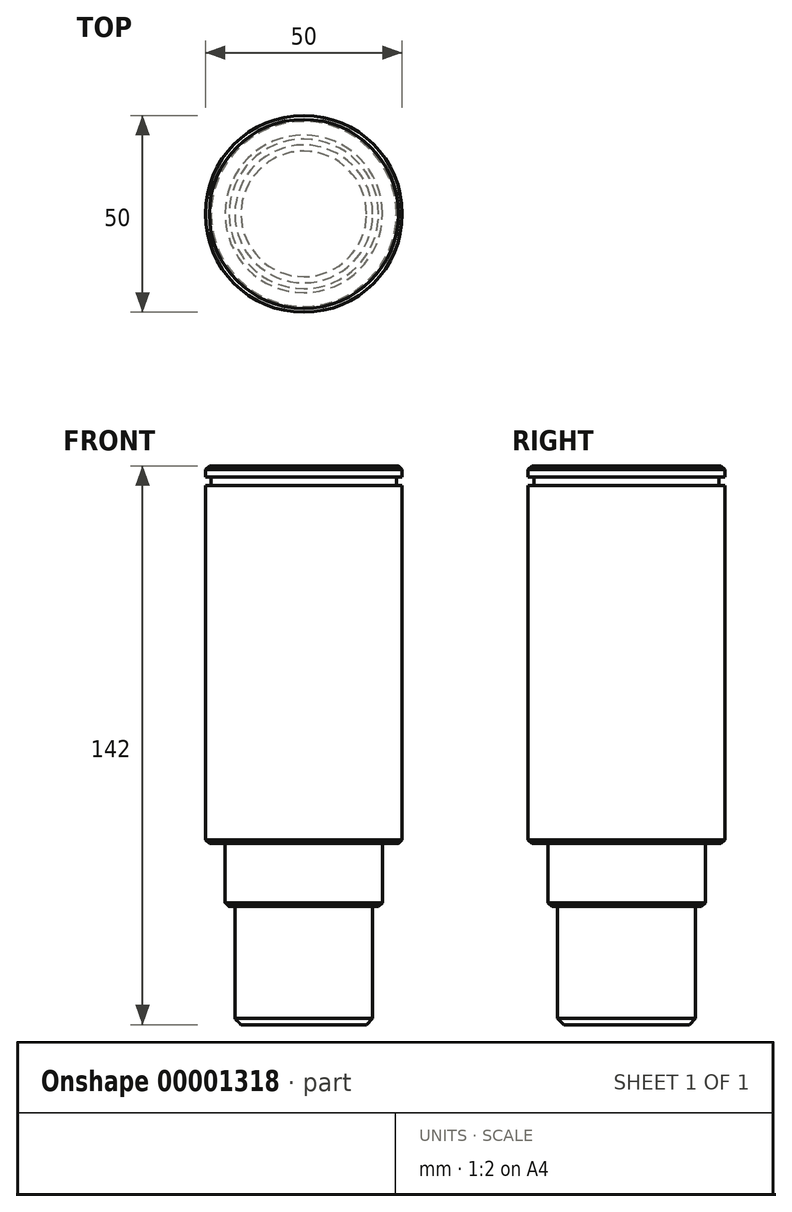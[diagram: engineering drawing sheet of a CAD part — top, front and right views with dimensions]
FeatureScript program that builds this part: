
annotation { "Feature Type Name" : "Feature", "Feature Type Description" : "" }
export const myFeature = defineFeature(function(context is Context, id is Id, definition is map)
    precondition{}
    {
        {
            var Q0;
            Q0=qCreatedBy(makeId("Top.planeOp"),FACE);
            var sketch = newSketch(context, id + "F0", { "sketchPlane" : qUnion([Q0])});
            skCircle(sketch, "E0", {"center": v(0, 0) * mm, "radius": 25 * mm});
            skSolve(sketch);
        }
        {
            var Q0;
            Q0=makeQuery(id+"F0.imprint","IMPRINT",FACE,{"disambiguationData":[TD([[makeQuery(id+"F0.imprint","IMPRINT",EDGE,{"derivedFrom":sQuery(id+"F0.wireOp",EDGE,"E0")}),1.0]])]});
            extrude(context, id + "F1", {"entities" : qUnion([Q0]), "depth" : 91 * mm});
        }
        {
            var Q0;
            Q0=makeQuery(id+"F1.opExtrude","CAP_FACE",FACE,{"disambiguationData":[OSD([sQuery(id+"F0.wireOp",EDGE,"E0")])],"isStart":false});
            var sketch = newSketch(context, id + "F2", { "sketchPlane" : qUnion([Q0])});
            skCircle(sketch, "E1", {"center": v(0, 0) * mm, "radius": 23.5 * mm});
            skSolve(sketch);
        }
        {
            var Q0;
            Q0=makeQuery(id+"F2.imprint","IMPRINT",FACE,{"disambiguationData":[TD([[makeQuery(id+"F2.imprint","IMPRINT",EDGE,{"derivedFrom":sQuery(id+"F2.wireOp",EDGE,"E1")}),1.0]])]});
            extrude(context, id + "F3", {"entities" : qUnion([Q0]), "operationType" : NewBodyOperationType.ADD, "depth" : 2.15 * mm});
        }
        {
            var Q0;
            Q0=makeQuery(id+"F3.opExtrude","CAP_FACE",FACE,{"disambiguationData":[OSD([sQuery(id+"F2.wireOp",EDGE,"E1")])],"isStart":false});
            var sketch = newSketch(context, id + "F4", { "sketchPlane" : qUnion([Q0])});
            skCircle(sketch, "E2", {"center": v(0, 0) * mm, "radius": 25 * mm});
            skSolve(sketch);
        }
        {
            var Q0;
            {var subQ0=makeQuery(id+"F4.imprint","IMPRINT",EDGE,{"derivedFrom":makeQuery(id+"F3.opExtrude","CAP_EDGE",EDGE,{"disambiguationData":[OSD([sQuery(id+"F2.wireOp",EDGE,"E1")])],"isStart":false})});Q0=qUnion([makeQuery(id+"F4.imprint","IMPRINT",FACE,{"disambiguationData":[TD([[makeQuery(id+"F4.imprint","IMPRINT",EDGE,{"derivedFrom":sQuery(id+"F4.wireOp",EDGE,"E2")}),1.0]])]}),makeQuery(id+"F4.imprint","IMPRINT",FACE,{"disambiguationData":[TD([[subQ0,1.0]])]})]);}
            extrude(context, id + "F5", {"entities" : qUnion([Q0]), "operationType" : NewBodyOperationType.ADD, "depth" : 2.85 * mm});
        }
        {
            var Q0;
            Q0=makeQuery(id+"F1.opExtrude","CAP_FACE",FACE,{"disambiguationData":[OSD([sQuery(id+"F0.wireOp",EDGE,"E0")])],"isStart":true});
            var sketch = newSketch(context, id + "F6", { "sketchPlane" : qUnion([Q0])});
            skCircle(sketch, "E3", {"center": v(0, 0) * mm, "radius": 20 * mm});
            skSolve(sketch);
        }
        {
            var Q0;
            Q0=makeQuery(id+"F6.imprint","IMPRINT",FACE,{"disambiguationData":[TD([[makeQuery(id+"F6.imprint","IMPRINT",EDGE,{"derivedFrom":sQuery(id+"F6.wireOp",EDGE,"E3")}),1.0]])]});
            extrude(context, id + "F7", {"entities" : qUnion([Q0]), "operationType" : NewBodyOperationType.ADD, "depth" : 16 * mm});
        }
        {
            var Q0;
            Q0=makeQuery(id+"F7.opExtrude","CAP_FACE",FACE,{"disambiguationData":[OSD([sQuery(id+"F6.wireOp",EDGE,"E3")])],"isStart":false});
            var sketch = newSketch(context, id + "F8", { "sketchPlane" : qUnion([Q0])});
            skCircle(sketch, "E4", {"center": v(0, 0) * mm, "radius": 17.5 * mm});
            skSolve(sketch);
        }
        {
            var Q0;
            Q0=makeQuery(id+"F8.imprint","IMPRINT",FACE,{"disambiguationData":[TD([[makeQuery(id+"F8.imprint","IMPRINT",EDGE,{"derivedFrom":sQuery(id+"F8.wireOp",EDGE,"E4")}),1.0]])]});
            extrude(context, id + "F9", {"entities" : qUnion([Q0]), "operationType" : NewBodyOperationType.ADD, "depth" : 30 * mm});
        }
        {
            var Q0;
            Q0=makeQuery(id+"F9.opExtrude","CAP_EDGE",EDGE,{"disambiguationData":[OSD([sQuery(id+"F8.wireOp",EDGE,"E4")])],"isStart":false});
            chamfer(context, id + "F10", {"entities" : qUnion([Q0]), "width" : 1.55 * mm, "tangentPropagation" : true});
        }
        {
            var Q0;
            Q0=makeQuery(id+"F7.opExtrude","CAP_EDGE",EDGE,{"disambiguationData":[OSD([sQuery(id+"F6.wireOp",EDGE,"E3")])],"isStart":false});
            var Q1;
            Q1=makeQuery(id+"F1.opExtrude","CAP_EDGE",EDGE,{"disambiguationData":[OSD([sQuery(id+"F0.wireOp",EDGE,"E0")])],"isStart":true});
            var Q2;
            Q2=makeQuery(id+"F5.opExtrude","CAP_EDGE",EDGE,{"disambiguationData":[OSD([sQuery(id+"F4.wireOp",EDGE,"E2")])],"isStart":false});
            chamfer(context, id + "F11", {"entities" : qUnion([Q0, Q1, Q2]), "width" : 1 * mm, "tangentPropagation" : true});
        }
    });
